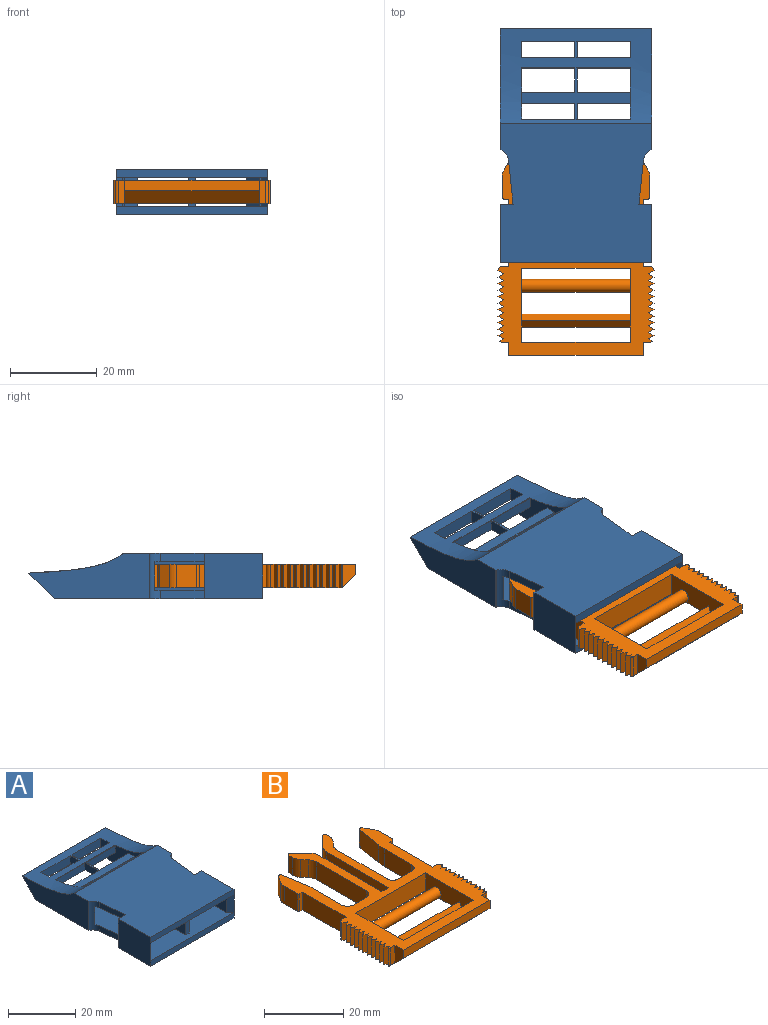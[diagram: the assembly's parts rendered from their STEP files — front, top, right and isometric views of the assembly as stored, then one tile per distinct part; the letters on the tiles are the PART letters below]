
ASSEMBLY  parts=2 mates=1
PART A: 58 faces, bbox 35x54x10.5 mm
  f0: plane 3.75x0.5mm, normal (0,0.06,1), area 1.9mm2, adj f2,f3,f37
  f1: plane 3.75x1mm, normal (0,-0.26,-0.97), area 1.9mm2, adj f2,f3,f7,f38
  f2: plane 3.75x3.3mm, normal (1,0,0), area 10.1mm2, adj f0,f1,f5,f28
  f3: plane 3.75x3.3mm, normal (-1,0,0), area 10.1mm2, adj f0,f1,f4,f29
  f4: plane 12.25x3.07mm, normal (0,-1,0), area 37.6mm2, adj f3,f26,f37,f38
  f5: plane 12.25x2.3mm, normal (0,1,0), area 28.1mm2, adj f2,f7,f25,f37
  f6: plane 25x11.93mm, normal (0,0,1), area 71.7mm2, adj f8,f9,f10,f11,f12,f13,f25,f26
  f7: plane 25x14.25mm, normal (0,0,-1), area 129.6mm2, adj f1,f5,f8,f9,f10,f11,f12,f13
  f8: plane 5.5x2.5mm, normal (1,0,0), area 13.7mm2, adj f6,f7,f10,f11
  f9: plane 5.5x2.5mm, normal (-1,0,0), area 13.7mm2, adj f6,f7,f34,f35
  f10: plane 12.25x2.5mm, normal (0,-1,0), area 30.6mm2, adj f6,f7,f8,f25
  f11: plane 12.25x2.5mm, normal (0,1,0), area 30.6mm2, adj f6,f7,f8,f25
  f12: plane 12.25x2.5mm, normal (0,-1,0), area 30.6mm2, adj f6,f7,f25,f56
  f13: plane 25x9.83mm, normal (0,1,0), area 91mm2, adj f6,f7,f20,f21,f23,f25,f26,f37
  f14: plane 35x2mm, normal (0,-1,0), area 70mm2, adj f17,f18,f20,f21
  f15: plane 6.5x0.4mm, normal (0,-1,0), area 2.6mm2, adj f21,f23,f31,f53
  f16: plane 27.93x10.5mm, normal (1,0,0), area 202mm2, adj f19,f20,f37,f38,f44
  f17: plane 13.5x10.5mm, normal (1,0,0), area 141.8mm2, adj f14,f19,f20,f30,f48,f54
  f18: plane 13.5x10.5mm, normal (-1,0,0), area 141.8mm2, adj f14,f19,f20,f30,f42,f55
  f19: plane 35x32.08mm, normal (0,0,1), area 1066.2mm2, adj f16,f17,f18,f27,f30,f37,f40,f41
  f20: plane 48x35mm, normal (0,0,-1), area 1248.5mm2, adj f13,f14,f16,f17,f18,f25,f26,f27
  f21: plane 35x33mm, normal (0,0,1), area 969.2mm2, adj f13,f14,f15,f22,f24,f25,f26,f31
  f22: plane 12x6.5mm, normal (-1,0,0), area 78mm2, adj f21,f23,f48,f54
  f23: plane 35x33mm, normal (0,0,-1), area 969.2mm2, adj f13,f15,f22,f24,f25,f26,f30,f31
  f24: plane 6.5x3.15mm, normal (1,0,0), area 20.5mm2, adj f21,f23,f33,f41
  f25: plane 19.91x10.02mm, normal (-1,0,0), area 125.2mm2, adj f5,f6,f7,f10,f11,f12,f13,f20
  f26: plane 19.91x10.02mm, normal (1,0,0), area 125.2mm2, adj f4,f6,f7,f13,f20,f21,f23,f29
  f27: plane 27.93x10.5mm, normal (-1,0,0), area 202mm2, adj f19,f20,f37,f38,f43
  f28: plane 12.25x3.07mm, normal (0,-1,0), area 37.6mm2, adj f2,f25,f37,f38
  f29: plane 12.25x2.3mm, normal (0,1,0), area 28.1mm2, adj f3,f7,f26,f37
  f30: plane 35x2mm, normal (0,-1,0), area 70mm2, adj f17,f18,f19,f23
  f31: plane 6.5x3.15mm, normal (-1,0,0), area 20.5mm2, adj f15,f21,f23,f45
  f32: plane 12x6.5mm, normal (1,0,0), area 78mm2, adj f21,f23,f42,f55
  f33: plane 6.5x0.4mm, normal (0,-1,0), area 2.6mm2, adj f21,f23,f24,f52
  f34: plane 12.25x2.5mm, normal (0,-1,0), area 30.6mm2, adj f6,f7,f9,f26
  f35: plane 12.25x2.5mm, normal (0,1,0), area 30.6mm2, adj f6,f7,f9,f26
  f36: plane 12.25x2.5mm, normal (0,-1,0), area 30.6mm2, adj f6,f7,f26,f57
  f37: extruded ~35x21.85mm, area 386.4mm2, adj f0,f4,f5,f6,f13,f16,f19,f25
  f38: plane 35x5.92mm, normal (0,0.71,-0.71), area 187.2mm2, adj f1,f4,f16,f20,f25,f26,f27,f28
  f39: plane 10.07x2mm, normal (-0.99,-0.1,0), area 20.2mm2, adj f20,f21,f41,f42
  f40: plane 10.07x2mm, normal (-0.99,-0.1,0), area 20.2mm2, adj f19,f23,f41,f42
  f41: cylinder r=3mm len=10.5mm, axis (0,0,1), area 24.6mm2, adj f19,f20,f21,f23,f24,f39,f40,f43
  f42: plane 10.5x3mm, normal (0,1,0), area 21.8mm2, adj f18,f19,f20,f21,f23,f32,f39,f40
  f43: plane 10.5x0.14mm, normal (-0.39,-0.92,0), area 1.6mm2, adj f19,f20,f27,f41
  f44: plane 10.5x0.14mm, normal (0.39,-0.92,0), area 1.6mm2, adj f16,f19,f20,f45
  f45: cylinder r=3mm len=10.5mm, axis (0,0,1), area 24.6mm2, adj f19,f20,f21,f23,f31,f44,f46,f47
  f46: plane 10.07x2mm, normal (0.99,-0.1,0), area 20.2mm2, adj f20,f21,f45,f48
  f47: plane 10.07x2mm, normal (0.99,-0.1,0), area 20.2mm2, adj f19,f23,f45,f48
  f48: plane 10.5x3mm, normal (0,1,0), area 21.8mm2, adj f17,f19,f20,f21,f22,f23,f46,f47
  f49: plane 31x6.5mm, normal (-1,0,0), area 201.5mm2, adj f13,f21,f23,f51
  f50: plane 31x6.5mm, normal (1,0,0), area 201.5mm2, adj f13,f21,f23,f51
  f51: plane 6.5x1.4mm, normal (0,-1,0), area 9.1mm2, adj f21,f23,f49,f50
  f52: plane 6.5x3.1mm, normal (0.71,-0.71,0), area 28.5mm2, adj f21,f23,f26,f33
  f53: plane 6.5x3.1mm, normal (-0.71,-0.71,0), area 28.5mm2, adj f15,f21,f23,f25
  f54: plane 6.5x1.5mm, normal (-0.71,-0.71,0), area 13.8mm2, adj f17,f21,f22,f23
  f55: plane 6.5x1.5mm, normal (0.71,-0.71,0), area 13.8mm2, adj f18,f21,f23,f32
  f56: plane 3.75x2.5mm, normal (1,0,0), area 9.4mm2, adj f6,f7,f12,f13
  f57: plane 3.75x2.5mm, normal (-1,0,0), area 9.4mm2, adj f6,f7,f13,f36
PART B: 110 faces, bbox 36x50.4x5.5 mm
  f0: plane 5.5x3mm, normal (-1,0,0), area 12mm2, adj f2,f53,f57,f84
  f1: plane 5.5x3mm, normal (1,0,0), area 12mm2, adj f2,f53,f57,f58
  f2: plane 31x2.5mm, normal (0,-1,0), area 77.5mm2, adj f0,f1,f53,f57
  f3: plane 47.42x36mm, normal (0,0,-1), area 618.6mm2, adj f4,f6,f7,f8,f9,f10,f11,f12
  f4: plane 17x5.5mm, normal (-1,0,0), area 82.5mm2, adj f3,f5,f52,f53,f54,f55,f56
  f5: plane 25x5.5mm, normal (0,1,0), area 137.5mm2, adj f4,f6,f53,f57
  f6: plane 17x5.5mm, normal (1,0,0), area 82.5mm2, adj f3,f5,f52,f53,f54,f55,f56
  f7: plane 5.5x2.4mm, normal (0,1,0), area 13.2mm2, adj f3,f8,f51,f53
  f8: plane 22.52x5.5mm, normal (1,0,0), area 123.9mm2, adj f3,f7,f9,f53
  f9: cylinder r=3mm len=5.5mm, axis (0,0,-1), area 13mm2, adj f3,f8,f10,f53
  f10: plane 5.5x3.63mm, normal (0.71,0.71,0), area 28.2mm2, adj f3,f9,f11,f53
  f11: cylinder r=0.5mm len=5.5mm, axis (0,0,-1), area 6.5mm2, adj f3,f10,f12,f53
  f12: plane 5.5x1.43mm, normal (-1,0,0), area 7.8mm2, adj f3,f11,f13,f53
  f13: cylinder r=3mm len=5.5mm, axis (0,0,-1), area 12mm2, adj f3,f12,f14,f53
  f14: plane 5.5x1.49mm, normal (-0.75,-0.67,0), area 11mm2, adj f3,f13,f15,f53
  f15: cylinder r=3mm len=5.5mm, axis (0,0,-1), area 12mm2, adj f3,f14,f16,f53
  f16: plane 18x5.5mm, normal (-1,0,0), area 99mm2, adj f3,f15,f17,f53
  f17: cylinder r=2mm len=5.5mm, axis (0,0,-1), area 17.3mm2, adj f3,f16,f18,f53
  f18: plane 5.5x4.8mm, normal (0,1,0), area 26.4mm2, adj f3,f17,f19,f53
  f19: cylinder r=2mm len=5.5mm, axis (0,0,-1), area 17.3mm2, adj f3,f18,f20,f53
  f20: plane 9.84x5.5mm, normal (1,0,0), area 54.1mm2, adj f3,f19,f21,f53
  f21: cylinder r=15mm len=5.5mm, axis (0,0,-1), area 12.7mm2, adj f3,f20,f22,f53
  f22: plane 7.76x5.5mm, normal (0.99,0.15,0), area 43.2mm2, adj f3,f21,f23,f53
  f23: cylinder r=0.7mm len=5.5mm, axis (0,0,-1), area 9.5mm2, adj f3,f22,f24,f53
  f24: plane 5.5x2.45mm, normal (-0.87,0.5,0), area 15.6mm2, adj f3,f23,f25,f53
  f25: cylinder r=3mm len=5.5mm, axis (0,0,-1), area 8.6mm2, adj f3,f24,f26,f53
  f26: plane 5.5x4.7mm, normal (-1,0,0), area 25.8mm2, adj f3,f25,f27,f53
  f27: cylinder r=0.5mm len=5.5mm, axis (0,0,-1), area 4.3mm2, adj f3,f26,f28,f53
  f28: plane 5.5x1mm, normal (0,-1,0), area 5.5mm2, adj f3,f27,f29,f53
  f29: plane 15.5x5.5mm, normal (-1,0,0), area 85.2mm2, adj f3,f28,f53,f87
  f30: plane 15.5x5.5mm, normal (1,0,0), area 85.2mm2, adj f3,f31,f53,f61
  f31: plane 5.5x1mm, normal (0,-1,0), area 5.5mm2, adj f3,f30,f32,f53
  f32: cylinder r=0.5mm len=5.5mm, axis (0,0,-1), area 4.3mm2, adj f3,f31,f33,f53
  f33: plane 5.5x4.7mm, normal (1,0,0), area 25.8mm2, adj f3,f32,f34,f53
  f34: cylinder r=3mm len=5.5mm, axis (0,0,-1), area 8.6mm2, adj f3,f33,f35,f53
  f35: plane 5.5x2.45mm, normal (0.87,0.5,0), area 15.6mm2, adj f3,f34,f36,f53
  f36: cylinder r=0.7mm len=5.5mm, axis (0,0,-1), area 9.5mm2, adj f3,f35,f37,f53
  f37: plane 7.76x5.5mm, normal (-0.99,0.15,0), area 43.2mm2, adj f3,f36,f38,f53
  f38: cylinder r=15mm len=5.5mm, axis (0,0,-1), area 12.7mm2, adj f3,f37,f39,f53
  f39: plane 9.84x5.5mm, normal (-1,0,0), area 54.1mm2, adj f3,f38,f40,f53
  f40: cylinder r=2mm len=5.5mm, axis (0,0,-1), area 17.3mm2, adj f3,f39,f41,f53
  f41: plane 5.5x4.8mm, normal (0,1,0), area 26.4mm2, adj f3,f40,f42,f53
  f42: cylinder r=2mm len=5.5mm, axis (0,0,-1), area 17.3mm2, adj f3,f41,f43,f53
  f43: plane 18x5.5mm, normal (1,0,0), area 99mm2, adj f3,f42,f44,f53
  f44: cylinder r=3mm len=5.5mm, axis (0,0,-1), area 12mm2, adj f3,f43,f45,f53
  f45: plane 5.5x1.49mm, normal (0.75,-0.67,0), area 11mm2, adj f3,f44,f46,f53
  f46: cylinder r=3mm len=5.5mm, axis (0,0,-1), area 12mm2, adj f3,f45,f47,f53
  f47: plane 5.5x1.16mm, normal (1,0,0), area 6.4mm2, adj f3,f46,f48,f53
  f48: cylinder r=0.5mm len=5.5mm, axis (0,0,-1), area 6.5mm2, adj f3,f47,f49,f53
  f49: plane 5.5x3.63mm, normal (-0.71,0.71,0), area 28.2mm2, adj f3,f48,f50,f53
  f50: cylinder r=3mm len=5.5mm, axis (0,0,-1), area 13mm2, adj f3,f49,f51,f53
  f51: plane 22.26x5.5mm, normal (-1,0,0), area 122.4mm2, adj f3,f7,f50,f53
  f52: plane 25x5.5mm, normal (0,-1,0), area 137.5mm2, adj f3,f4,f6,f53
  f53: plane 50.42x36mm, normal (0,0,1), area 636.6mm2, adj f0,f1,f2,f4,f5,f6,f7,f8
  f54: plane 25x2.6mm, normal (0,0.87,0.5), area 75mm2, adj f3,f4,f6,f55
  f55: plane 25x2.6mm, normal (0,-0.87,0.5), area 75mm2, adj f3,f4,f6,f54
  f56: cylinder r=1.5mm len=25mm, axis (-1,0,0), area 235.6mm2, adj f4,f6
  f57: plane 31x3mm, normal (0,-0.71,-0.71), area 131.5mm2, adj f0,f1,f2,f3,f5
  f58: plane 5.5x1.5mm, normal (0,-1,0), area 8.2mm2, adj f1,f3,f53,f59
  f59: cylinder r=1mm len=5.5mm, axis (0,0,1), area 3.7mm2, adj f3,f53,f58,f81
  f60: cylinder r=1mm len=5.5mm, axis (0,0,1), area 8.6mm2, adj f3,f53,f61,f82
  f61: plane 5.5x1.5mm, normal (0,1,0), area 8.2mm2, adj f3,f30,f53,f60
  f62: plane 5.5x1.3mm, normal (0.5,-0.87,0), area 8.2mm2, adj f3,f53,f63,f79
  f63: plane 5.5x1.3mm, normal (0.5,0.87,0), area 8.2mm2, adj f3,f53,f62,f80
  f64: plane 5.5x1.3mm, normal (0.5,-0.87,0), area 8.2mm2, adj f3,f53,f65,f77
  f65: plane 5.5x1.3mm, normal (0.5,0.87,0), area 8.2mm2, adj f3,f53,f64,f78
  f66: plane 5.5x1.3mm, normal (0.5,-0.87,0), area 8.2mm2, adj f3,f53,f67,f75
  f67: plane 5.5x1.3mm, normal (0.5,0.87,0), area 8.2mm2, adj f3,f53,f66,f76
  f68: plane 5.5x1.3mm, normal (0.5,-0.87,0), area 8.2mm2, adj f3,f53,f69,f73
  f69: plane 5.5x1.3mm, normal (0.5,0.87,0), area 8.2mm2, adj f3,f53,f68,f74
  f70: plane 5.5x1.3mm, normal (0.5,-0.87,0), area 8.2mm2, adj f3,f53,f71,f83
  f71: plane 5.5x1.3mm, normal (0.5,0.87,0), area 8.2mm2, adj f3,f53,f70,f72
  f72: plane 5.5x1.3mm, normal (0.5,-0.87,0), area 8.2mm2, adj f3,f53,f71,f73
  f73: plane 5.5x1.3mm, normal (0.5,0.87,0), area 8.2mm2, adj f3,f53,f68,f72
  f74: plane 5.5x1.3mm, normal (0.5,-0.87,0), area 8.2mm2, adj f3,f53,f69,f75
  f75: plane 5.5x1.3mm, normal (0.5,0.87,0), area 8.2mm2, adj f3,f53,f66,f74
  f76: plane 5.5x1.3mm, normal (0.5,-0.87,0), area 8.2mm2, adj f3,f53,f67,f77
  f77: plane 5.5x1.3mm, normal (0.5,0.87,0), area 8.2mm2, adj f3,f53,f64,f76
  f78: plane 5.5x1.3mm, normal (0.5,-0.87,0), area 8.2mm2, adj f3,f53,f65,f79
  f79: plane 5.5x1.3mm, normal (0.5,0.87,0), area 8.2mm2, adj f3,f53,f62,f78
  f80: plane 5.5x1.3mm, normal (0.5,-0.87,0), area 8.2mm2, adj f3,f53,f63,f81
  f81: plane 5.5x0.92mm, normal (0.5,0.87,0), area 5.9mm2, adj f3,f53,f59,f80
  f82: plane 5.5x1.3mm, normal (0.5,-0.87,0), area 8.2mm2, adj f3,f53,f60,f83
  f83: plane 5.5x1.3mm, normal (0.5,0.87,0), area 8.2mm2, adj f3,f53,f70,f82
  f84: plane 5.5x1.5mm, normal (0,-1,0), area 8.2mm2, adj f0,f3,f53,f85
  f85: cylinder r=1mm len=5.5mm, axis (0,0,1), area 3.7mm2, adj f3,f53,f84,f107
  f86: cylinder r=1mm len=5.5mm, axis (0,0,1), area 8.6mm2, adj f3,f53,f87,f108
  f87: plane 5.5x1.5mm, normal (0,1,0), area 8.2mm2, adj f3,f29,f53,f86
  f88: plane 5.5x1.3mm, normal (-0.5,-0.87,0), area 8.2mm2, adj f3,f53,f89,f105
  f89: plane 5.5x1.3mm, normal (-0.5,0.87,0), area 8.2mm2, adj f3,f53,f88,f106
  f90: plane 5.5x1.3mm, normal (-0.5,-0.87,0), area 8.2mm2, adj f3,f53,f91,f103
  f91: plane 5.5x1.3mm, normal (-0.5,0.87,0), area 8.2mm2, adj f3,f53,f90,f104
  f92: plane 5.5x1.3mm, normal (-0.5,-0.87,0), area 8.2mm2, adj f3,f53,f93,f101
  f93: plane 5.5x1.3mm, normal (-0.5,0.87,0), area 8.2mm2, adj f3,f53,f92,f102
  f94: plane 5.5x1.3mm, normal (-0.5,-0.87,0), area 8.2mm2, adj f3,f53,f95,f99
  f95: plane 5.5x1.3mm, normal (-0.5,0.87,0), area 8.2mm2, adj f3,f53,f94,f100
  f96: plane 5.5x1.3mm, normal (-0.5,-0.87,0), area 8.2mm2, adj f3,f53,f97,f109
  f97: plane 5.5x1.3mm, normal (-0.5,0.87,0), area 8.2mm2, adj f3,f53,f96,f98
  f98: plane 5.5x1.3mm, normal (-0.5,-0.87,0), area 8.2mm2, adj f3,f53,f97,f99
  f99: plane 5.5x1.3mm, normal (-0.5,0.87,0), area 8.2mm2, adj f3,f53,f94,f98
  f100: plane 5.5x1.3mm, normal (-0.5,-0.87,0), area 8.2mm2, adj f3,f53,f95,f101
  f101: plane 5.5x1.3mm, normal (-0.5,0.87,0), area 8.2mm2, adj f3,f53,f92,f100
  f102: plane 5.5x1.3mm, normal (-0.5,-0.87,0), area 8.2mm2, adj f3,f53,f93,f103
  f103: plane 5.5x1.3mm, normal (-0.5,0.87,0), area 8.2mm2, adj f3,f53,f90,f102
  f104: plane 5.5x1.3mm, normal (-0.5,-0.87,0), area 8.2mm2, adj f3,f53,f91,f105
  f105: plane 5.5x1.3mm, normal (-0.5,0.87,0), area 8.2mm2, adj f3,f53,f88,f104
  f106: plane 5.5x1.3mm, normal (-0.5,-0.87,0), area 8.2mm2, adj f3,f53,f89,f107
  f107: plane 5.5x0.92mm, normal (-0.5,0.87,0), area 5.9mm2, adj f3,f53,f85,f106
  f108: plane 5.5x1.3mm, normal (-0.5,-0.87,0), area 8.2mm2, adj f3,f53,f86,f109
  f109: plane 5.5x1.3mm, normal (-0.5,0.87,0), area 8.2mm2, adj f3,f53,f96,f108
PLACE A at identity fixed
PLACE B t=(0,-23.97,2.5)mm
MATE slider A.f51 <-> B.f7  axis (0,-1,0) through (0,-25,5.25)mm
